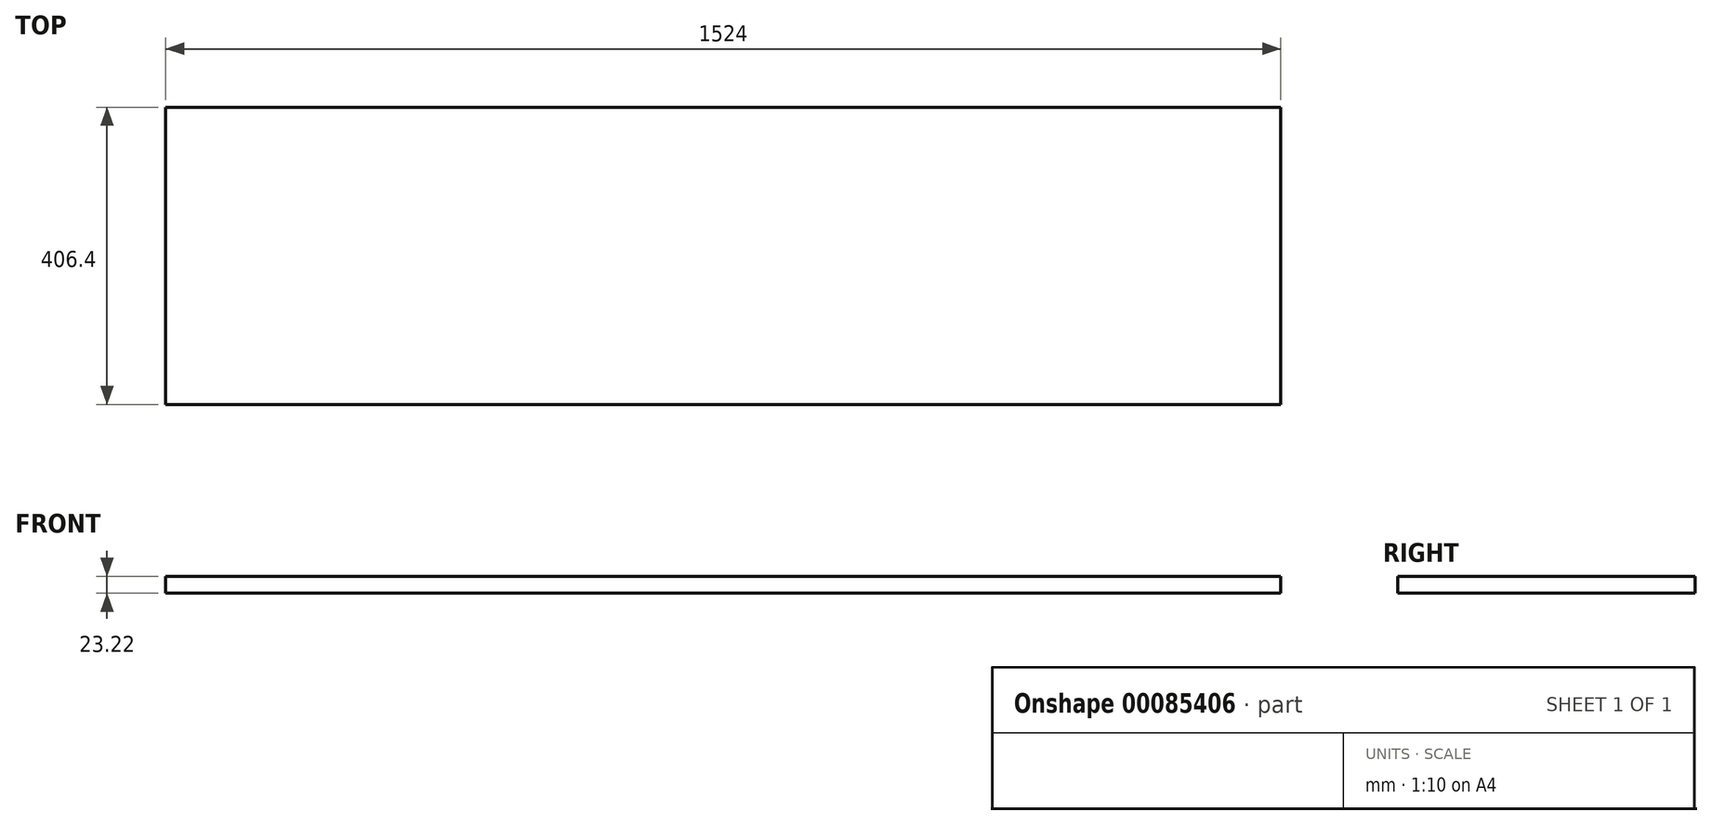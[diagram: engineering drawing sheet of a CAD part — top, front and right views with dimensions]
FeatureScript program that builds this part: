
annotation { "Feature Type Name" : "Feature", "Feature Type Description" : "" }
export const myFeature = defineFeature(function(context is Context, id is Id, definition is map)
    precondition{}
    {
        {
            var Q0;
            Q0=qCreatedBy(makeId("Right.planeOp"),FACE);
            var sketch = newSketch(context, id + "F0", { "sketchPlane" : qUnion([Q0])});
            skLineSegment(sketch, "E0.bottom", {"start": v(0, 0) * mm, "end": v(406.4, 0) * mm});
            skLineSegment(sketch, "E0.top", {"start": v(0, -23.22) * mm, "end": v(406.4, -23.22) * mm});
            skLineSegment(sketch, "E0.left", {"start": v(0, 0) * mm, "end": v(0, -23.22) * mm});
            skLineSegment(sketch, "E0.right", {"start": v(406.4, 0) * mm, "end": v(406.4, -23.22) * mm});
            skSolve(sketch);
        }
        {
            var Q0;
            Q0=makeQuery(id+"F0.imprint","IMPRINT",FACE,{"disambiguationData":[TD([[makeQuery(id+"F0.imprint","IMPRINT",EDGE,{"derivedFrom":sQuery(id+"F0.wireOp",EDGE,"E0.bottom")}),-1.0]])]});
            extrude(context, id + "F1", {"entities" : qUnion([Q0]), "oppositeDirection" : true, "depth" : 762 * mm});
        }
        {
            var Q0;
            Q0=makeQuery(id+"F1.opExtrude","SWEPT_BODY",BODY,{"disambiguationData":[OSD([sQuery(id+"F0.wireOp",EDGE,"E0.bottom"),sQuery(id+"F0.wireOp",EDGE,"E0.top"),sQuery(id+"F0.wireOp",EDGE,"E0.left"),sQuery(id+"F0.wireOp",EDGE,"E0.right")])]});
            var Q1;
            Q1=qCreatedBy(makeId("Right.planeOp"),FACE);
            mirror(context, id + "F2", {"operationType" : NewBodyOperationType.ADD, "entities" : qUnion([Q0]), "mirrorPlane" : qUnion([Q1])});
        }
    });
